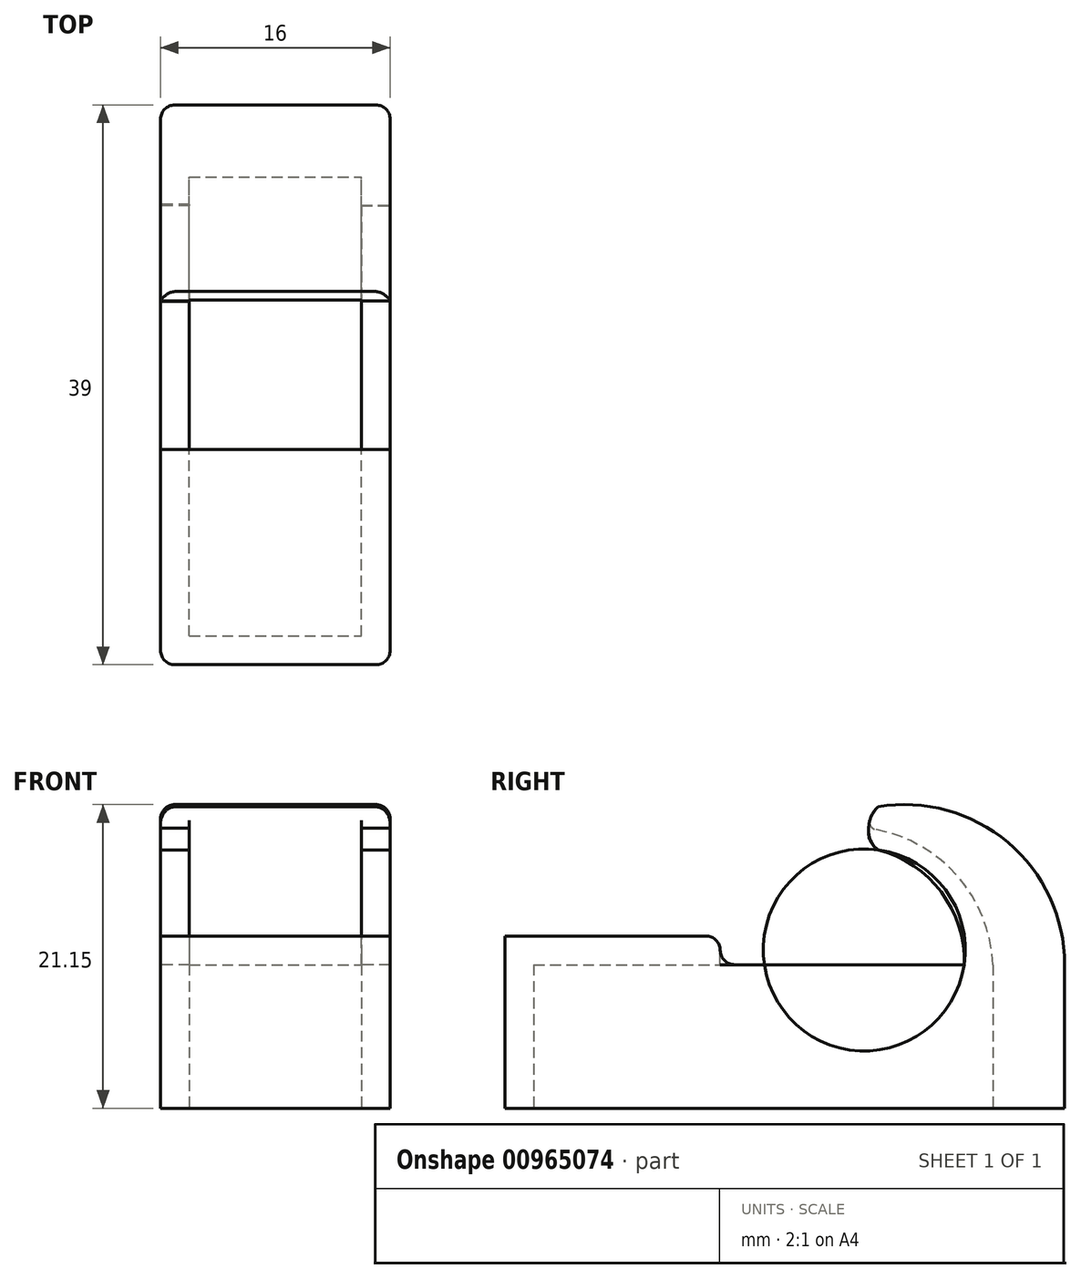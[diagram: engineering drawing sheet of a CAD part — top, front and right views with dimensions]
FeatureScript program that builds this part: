
annotation { "Feature Type Name" : "Feature", "Feature Type Description" : "" }
export const myFeature = defineFeature(function(context is Context, id is Id, definition is map)
    precondition{}
    {
        {
            var Q0;
            Q0=qCreatedBy(makeId("Top.planeOp"),FACE);
            var sketch = newSketch(context, id + "F0", { "sketchPlane" : qUnion([Q0])});
            skLineSegment(sketch, "E0.bottom", {"start": v(0, 0) * mm, "end": v(12, 0) * mm});
            skLineSegment(sketch, "E0.top", {"start": v(0, 32) * mm, "end": v(12, 32) * mm});
            skLineSegment(sketch, "E0.left", {"start": v(0, 0) * mm, "end": v(0, 32) * mm});
            skLineSegment(sketch, "E0.right", {"start": v(12, 0) * mm, "end": v(12, 32) * mm});
            skLineSegment(sketch, "E1.bottom", {"start": v(-2, 37) * mm, "end": v(14, 37) * mm});
            skLineSegment(sketch, "E1.top", {"start": v(-2, -2) * mm, "end": v(14, -2) * mm});
            skLineSegment(sketch, "E1.left", {"start": v(-2, 37) * mm, "end": v(-2, -2) * mm});
            skLineSegment(sketch, "E1.right", {"start": v(14, 37) * mm, "end": v(14, -2) * mm});
            skSolve(sketch);
        }
        {
            var Q0;
            Q0=makeQuery(id+"F0.imprint","IMPRINT",FACE,{"disambiguationData":[TD([[makeQuery(id+"F0.imprint","IMPRINT",EDGE,{"derivedFrom":sQuery(id+"F0.wireOp",EDGE,"E0.bottom")}),-1.0]])]});
            extrude(context, id + "F1", {"entities" : qUnion([Q0]), "depth" : 10 * mm, "offsetDistance" : 25 * mm});
        }
        {
            var Q0;
            Q0=makeQuery(id+"F1.opExtrude","SWEPT_FACE",FACE,{"disambiguationData":[OSD([sQuery(id+"F0.wireOp",EDGE,"E1.left")])]});
            cPlane(context, id + "F2", {"entities" : qUnion([Q0]), "cplaneType" : CPlaneType.OFFSET, "offset" : 8 * mm, "oppositeDirection" : true, "width" : 150 * mm, "height" : 150 * mm});
        }
        {
            var Q0;
            Q0=qCreatedBy(id+"F2.planeOp",FACE);
            var sketch = newSketch(context, id + "F3", { "sketchPlane" : qUnion([Q0])});
            skArc(sketch, "E2", {"start": v(-24, 21) * mm, "mid": v(-33.05, 18.51) * mm, "end": v(-37, 10) * mm});
            skArc(sketch, "E3", {"start": v(-24, 18) * mm, "mid": v(-28.4, 15.05) * mm, "end": v(-30, 10) * mm});
            skArc(sketch, "E4", {"start": v(-24, 18) * mm, "mid": v(-23.35, 19.5) * mm, "end": v(-24, 21) * mm});
            skArc(sketch, "E5", {"start": v(-23.35, 19.5) * mm, "mid": v(-29.4, 16.32) * mm, "end": v(-32, 10) * mm});
            skLineSegment(sketch, "E6", {"start": v(-30, 10) * mm, "end": v(-32, 10) * mm});
            skLineSegment(sketch, "E7", {"start": v(-32, 10) * mm, "end": v(-37, 10) * mm});
            skSolve(sketch);
        }
        {
            var Q0;
            {var subQ0=sQuery(id+"F3.wireOp",EDGE,"E2");Q0=makeQuery(id+"F3.imprint","IMPRINT",FACE,{"disambiguationData":[TD([[makeQuery(id+"F3.imprint","IMPRINT",EDGE,{"derivedFrom":subQ0}),1.0]])]});}
            extrude(context, id + "F4", {"entities" : qUnion([Q0]), "operationType" : NewBodyOperationType.ADD, "endBound" : BoundingType.SYMMETRIC, "oppositeDirection" : true, "depth" : 16 * mm, "offsetDistance" : 25 * mm});
        }
        {
            var Q0;
            Q0=makeQuery(id+"F4.boolean.opBoolean","MERGE",FACE,{"derivedFrom":[makeQuery(id+"F1.opExtrude","SWEPT_FACE",FACE,{"disambiguationData":[OSD([sQuery(id+"F0.wireOp",EDGE,"E1.left")])]}),makeQuery(id+"F4.opExtrude","CAP_FACE",FACE,{"disambiguationData":[OSD([sQuery(id+"F3.wireOp",EDGE,"E2"),sQuery(id+"F3.wireOp",EDGE,"E4"),sQuery(id+"F3.wireOp",EDGE,"E5"),sQuery(id+"F3.wireOp",EDGE,"E7")])],"isStart":true})]});
            var sketch = newSketch(context, id + "F5", { "sketchPlane" : qUnion([Q0])});
            skArc(sketch, "E8", {"start": v(-23.35, 19.5) * mm, "mid": v(-29.67, 16.57) * mm, "end": v(-32, 10) * mm});
            skArc(sketch, "E9", {"start": v(-24, 18) * mm, "mid": v(-23.45, 18.65) * mm, "end": v(-23.35, 19.5) * mm});
            skArc(sketch, "E10", {"start": v(-24, 18) * mm, "mid": v(-28.67, 15.25) * mm, "end": v(-30, 10) * mm});
            skLineSegment(sketch, "E11", {"start": v(-30, 10) * mm, "end": v(-32, 10) * mm});
            skLineSegment(sketch, "E12.bottom", {"start": v(2, 10) * mm, "end": v(-13, 10) * mm});
            skLineSegment(sketch, "E12.top", {"start": v(2, 12) * mm, "end": v(-13, 12) * mm});
            skLineSegment(sketch, "E12.left", {"start": v(2, 10) * mm, "end": v(2, 12) * mm});
            skLineSegment(sketch, "E12.right", {"start": v(-13, 10) * mm, "end": v(-13, 12) * mm});
            skSolve(sketch);
        }
        {
            var Q0;
            Q0=makeQuery(id+"F5.imprint","IMPRINT",FACE,{"disambiguationData":[TD([[makeQuery(id+"F5.imprint","IMPRINT",EDGE,{"derivedFrom":sQuery(id+"F5.wireOp",EDGE,"E8")}),1.0]])]});
            var Q1;
            {var subQ0=sQuery(id+"F5.wireOp",EDGE,"E9");Q1=makeQuery(id+"F5.imprint","IMPRINT",FACE,{"disambiguationData":[TD([[makeQuery(id+"F5.imprint","IMPRINT",EDGE,{"derivedFrom":subQ0}),1.0]])]});}
            var Q2;
            {var subQ0=sQuery(id+"F5.wireOp",EDGE,"MAJ1SbT8-xYG6-ZxgM-nbvt-HSJhpmXW56Eo.bottom");var subQ1=sQuery(id+"F5.wireOp",EDGE,"E10");var subQ2=makeQuery(id+"F5.imprint","INTERSECT",VERTEX,{"derivedFrom":[subQ1,subQ0]});Q2=makeQuery(id+"F5.imprint","IMPRINT",FACE,{"disambiguationData":[TD([[makeQuery(id+"F5.imprint","IMPRINT",EDGE,{"disambiguationData":[TD([[subQ2,1.0]])],"derivedFrom":subQ1}),-1.0]])]});}
            extrude(context, id + "F6", {"entities" : qUnion([Q0, Q1, Q2]), "operationType" : NewBodyOperationType.ADD, "oppositeDirection" : true, "depth" : 2 * mm, "offsetDistance" : 25 * mm});
        }
        {
            var Q0;
            Q0=makeQuery(id+"F4.boolean.opBoolean","MERGE",FACE,{"derivedFrom":[makeQuery(id+"F1.opExtrude","SWEPT_FACE",FACE,{"disambiguationData":[OSD([sQuery(id+"F0.wireOp",EDGE,"E1.right")])]}),makeQuery(id+"F4.opExtrude","CAP_FACE",FACE,{"disambiguationData":[OSD([sQuery(id+"F3.wireOp",EDGE,"E2"),sQuery(id+"F3.wireOp",EDGE,"E4"),sQuery(id+"F3.wireOp",EDGE,"E5"),sQuery(id+"F3.wireOp",EDGE,"E7")])],"isStart":false})]});
            var sketch = newSketch(context, id + "F7", { "sketchPlane" : qUnion([Q0])});
            skArc(sketch, "E13", {"start": v(32, 10) * mm, "mid": v(29.4, 16.32) * mm, "end": v(23.35, 19.5) * mm});
            skArc(sketch, "E14", {"start": v(30, 10) * mm, "mid": v(28.4, 15.05) * mm, "end": v(24, 18) * mm});
            skLineSegment(sketch, "E15", {"start": v(30, 10) * mm, "end": v(32, 10) * mm});
            skArc(sketch, "E16", {"start": v(23.35, 19.5) * mm, "mid": v(23.48, 18.67) * mm, "end": v(24, 18) * mm});
            skLineSegment(sketch, "E17.bottom", {"start": v(32, 10) * mm, "end": v(-2, 10) * mm});
            skLineSegment(sketch, "E17.top", {"start": v(32, 12) * mm, "end": v(-2, 12) * mm});
            skLineSegment(sketch, "E17.left", {"start": v(32, 10) * mm, "end": v(32, 12) * mm});
            skLineSegment(sketch, "E17.right", {"start": v(-2, 10) * mm, "end": v(-2, 12) * mm});
            skSolve(sketch);
        }
        {
            var Q0;
            Q0=makeQuery(id+"F7.imprint","IMPRINT",FACE,{"disambiguationData":[TD([[makeQuery(id+"F7.imprint","IMPRINT",EDGE,{"derivedFrom":sQuery(id+"F7.wireOp",EDGE,"E13")}),-1.0]])]});
            extrude(context, id + "F8", {"entities" : qUnion([Q0]), "operationType" : NewBodyOperationType.ADD, "oppositeDirection" : true, "depth" : 2 * mm, "offsetDistance" : 25 * mm});
        }
        {
            var Q0;
            Q0=makeQuery(id+"F8.boolean.opBoolean","SPLIT",EDGE,{"derivedFrom":makeQuery(id+"F6.boolean.opBoolean","SPLIT",EDGE,{"derivedFrom":makeQuery(id+"F4.opExtrude","SWEPT_EDGE",EDGE,{"disambiguationData":[OSD([sQuery(id+"F3.wireOp",EDGE,"E4"),sQuery(id+"F3.wireOp",EDGE,"E5")])]})})});
            fillet(context, id + "F9", {"entities" : qUnion([Q0]), "tangentPropagation" : true, "radius" : 0.5 * mm, "defaultsChanged" : true, "vertexSettings" : [], "allowEdgeOverflow" : false});
        }
        {
            var Q0;
            {var subQ5=sQuery(id+"F5.wireOp",EDGE,"MAJ1SbT8-xYG6-ZxgM-nbvt-HSJhpmXW56Eo.right");Q0=makeQuery(id+"F5.imprint","IMPRINT",FACE,{"disambiguationData":[TD([[makeQuery(id+"F5.imprint","IMPRINT",EDGE,{"derivedFrom":subQ5}),1.0]])]});}
            var Q1;
            Q1=makeQuery(id+"F5.imprint","IMPRINT",FACE,{"disambiguationData":[TD([[makeQuery(id+"F5.imprint","IMPRINT",EDGE,{"derivedFrom":sQuery(id+"F5.wireOp",EDGE,"E12.bottom")}),1.0]])]});
            extrude(context, id + "F10", {"entities" : qUnion([Q0, Q1]), "operationType" : NewBodyOperationType.ADD, "oppositeDirection" : true, "depth" : 16 * mm, "offsetDistance" : 25 * mm});
        }
        {
            var Q0;
            Q0=makeQuery(id+"F1.opExtrude","SWEPT_EDGE",EDGE,{"disambiguationData":[OSD([sQuery(id+"F0.wireOp",EDGE,"E1.top"),sQuery(id+"F0.wireOp",EDGE,"E1.left")])]});
            var Q1;
            Q1=makeQuery(id+"F1.opExtrude","SWEPT_EDGE",EDGE,{"disambiguationData":[OSD([sQuery(id+"F0.wireOp",EDGE,"E1.top"),sQuery(id+"F0.wireOp",EDGE,"E1.right")])]});
            var Q2;
            Q2=makeQuery(id+"F1.opExtrude","SWEPT_EDGE",EDGE,{"disambiguationData":[OSD([sQuery(id+"F0.wireOp",EDGE,"E1.bottom"),sQuery(id+"F0.wireOp",EDGE,"E1.left")])]});
            var Q3;
            Q3=makeQuery(id+"F1.opExtrude","SWEPT_EDGE",EDGE,{"disambiguationData":[OSD([sQuery(id+"F0.wireOp",EDGE,"E1.bottom"),sQuery(id+"F0.wireOp",EDGE,"E1.right")])]});
            var Q4;
            {var subQ0=sQuery(id+"F5.wireOp",EDGE,"E12.right");var subQ1=sQuery(id+"F5.wireOp",EDGE,"E12.bottom");var subQ2=sQuery(id+"F0.wireOp",EDGE,"E1.left");var subQ3=sQuery(id+"F0.wireOp",EDGE,"E0.left");var subQ4=makeQuery(id+"F1.opExtrude","CAP_FACE",FACE,{"disambiguationData":[OSD([sQuery(id+"F0.wireOp",EDGE,"E0.bottom"),sQuery(id+"F0.wireOp",EDGE,"E0.top"),subQ3,sQuery(id+"F0.wireOp",EDGE,"E0.right"),sQuery(id+"F0.wireOp",EDGE,"E1.bottom"),sQuery(id+"F0.wireOp",EDGE,"E1.top"),subQ2,sQuery(id+"F0.wireOp",EDGE,"E1.right")])],"isStart":false});var subQ9=makeQuery(id+"F10.opExtrude","SWEPT_FACE",FACE,{"disambiguationData":[OSD([subQ0])]});Q4=makeQuery(id+"F10.boolean.opBoolean","SPLIT",EDGE,{"disambiguationData":[topologyDisambiguationEdgeConnected([subQ4,subQ9]),TD([makeQuery(id+"F1.opExtrude","SWEPT_FACE",FACE,{"disambiguationData":[OSD([subQ3])]})])],"derivedFrom":makeQuery(id+"F10.opExtrude","SWEPT_EDGE",EDGE,{"disambiguationData":[OSD([subQ2,subQ1,subQ0])]})});}
            var Q5;
            Q5=makeQuery(id+"F10.opExtrude","SWEPT_EDGE",EDGE,{"disambiguationData":[OSD([sQuery(id+"F5.wireOp",EDGE,"E12.top"),sQuery(id+"F5.wireOp",EDGE,"E12.right")])]});
            var Q6;
            {var subQ0=sQuery(id+"F5.wireOp",EDGE,"E12.right");var subQ1=sQuery(id+"F5.wireOp",EDGE,"E12.bottom");var subQ2=sQuery(id+"F0.wireOp",EDGE,"E1.right");var subQ3=sQuery(id+"F0.wireOp",EDGE,"E0.right");var subQ8=sQuery(id+"F0.wireOp",EDGE,"E1.left");var subQ9=makeQuery(id+"F1.opExtrude","CAP_FACE",FACE,{"disambiguationData":[OSD([sQuery(id+"F0.wireOp",EDGE,"E0.bottom"),sQuery(id+"F0.wireOp",EDGE,"E0.top"),sQuery(id+"F0.wireOp",EDGE,"E0.left"),subQ3,sQuery(id+"F0.wireOp",EDGE,"E1.bottom"),sQuery(id+"F0.wireOp",EDGE,"E1.top"),subQ8,subQ2])],"isStart":false});var subQ10=makeQuery(id+"F10.opExtrude","SWEPT_FACE",FACE,{"disambiguationData":[OSD([subQ0])]});Q6=makeQuery(id+"F10.boolean.opBoolean","SPLIT",EDGE,{"disambiguationData":[topologyDisambiguationEdgeConnected([subQ9,subQ10]),TD([makeQuery(id+"F1.opExtrude","SWEPT_FACE",FACE,{"disambiguationData":[OSD([subQ3])]})])],"derivedFrom":makeQuery(id+"F10.opExtrude","SWEPT_EDGE",EDGE,{"disambiguationData":[OSD([subQ8,subQ1,subQ0])]})});}
            fillet(context, id + "F11", {"entities" : qUnion([Q0, Q1, Q2, Q3, Q4, Q5, Q6]), "tangentPropagation" : true, "radius" : 1 * mm, "defaultsChanged" : false, "vertexSettings" : [], "allowEdgeOverflow" : false});
        }
    });
